# Revit family: Sanitary_Toilet-Cisterns_DURAVIT-AG_D-Code-tank-094010ed
name_source: partatom
category: Plumbing Fixtures
revit_build: Autodesk Revit 2018 (Build: 20190510_1515(x64)
units: mm (PartAtom-declared; Revit-internal decimal feet)

## family parameters
Always vertical = No
Cut with Voids When Loaded = No
OmniClass Number = 23.31.19.19.19
OmniClass Title = Water Closet Tanks
Part Type = Normal
Room Calculation Point = No
Round Connector Dimension = Use Diameter
Shared = No
Work Plane-Based = Yes

## types (1)
- D-Code tank - 094010
    BIMobject category = Toilet Cisterns
    Connector Description = Water inlet
    Date of publishing = 08.09.2020 00:00:00
    Default Elevation = 1219.2 mm  [stored 4 ft]
    Description = Duravit D-Code Cistern White, Incl. mechanism, 3 l / 6 l, Dual Flush, Bottom left, 3/8'' - 0940100004
    ETIM classification = EC010204 | Accessories, shower/WC
    Edition number = 1
    IFC Classification = Sanitary Terminal
    Inlet Diameter = 10 mm
    Installation instructions = https://pro.duravit.com
    Main material = Duravit - Metal - 00 - White Alpin
    Manufacturer = Duravit
    Manufacturer name = DURAVIT AG
    Masterformat 2014 Code = 22 41 13
    Masterformat 2014 Description = Residential Water Closets, Urinals, and Bidets
    Material main = Ceramics
    Model = D-Code tank - 094010
    OmniClass Code = 23-31 19 19 19
    OmniClass Description = Water Closet Tanks
    Product Guid = 6c946cb8-a588-432d-9300-e8e031bf3e65
    Product SKU = d-code-tank-094010
    Product certification = https://pro.duravit.com
    Product data url = https://bimobject.com
    Product family = Bathtubs & Wellbeing
    Product group = Cistern
    Product name = D-Code tank - 094010
    Product url = https://pro.duravit.com
    QR code = https://bimobject.com
    Secondary material = Duravit - Glass - Frosted
    Technical description = https://pro.duravit.com
    UNSPSC Code = 301815
    URL = https://www.duravit.com
    Uniclass 2015 Code = Pr_40_20_93_89
    Uniclass 2015 Name = WC cisterns
    Uniformat II Code = D2010
    Uniformat II Description = Plumbing Fixtures
    Weight Net (Kg) = 13,35
    Youtube clip = https://pro.duravit.com

note: [stored X ft] marks values corroborated as IEEE doubles in the binary element streams (Revit-internal decimal feet)

## geometry (parser evidence)
native form markers: Sweep x3
no freeform markers — native parametric forms only
